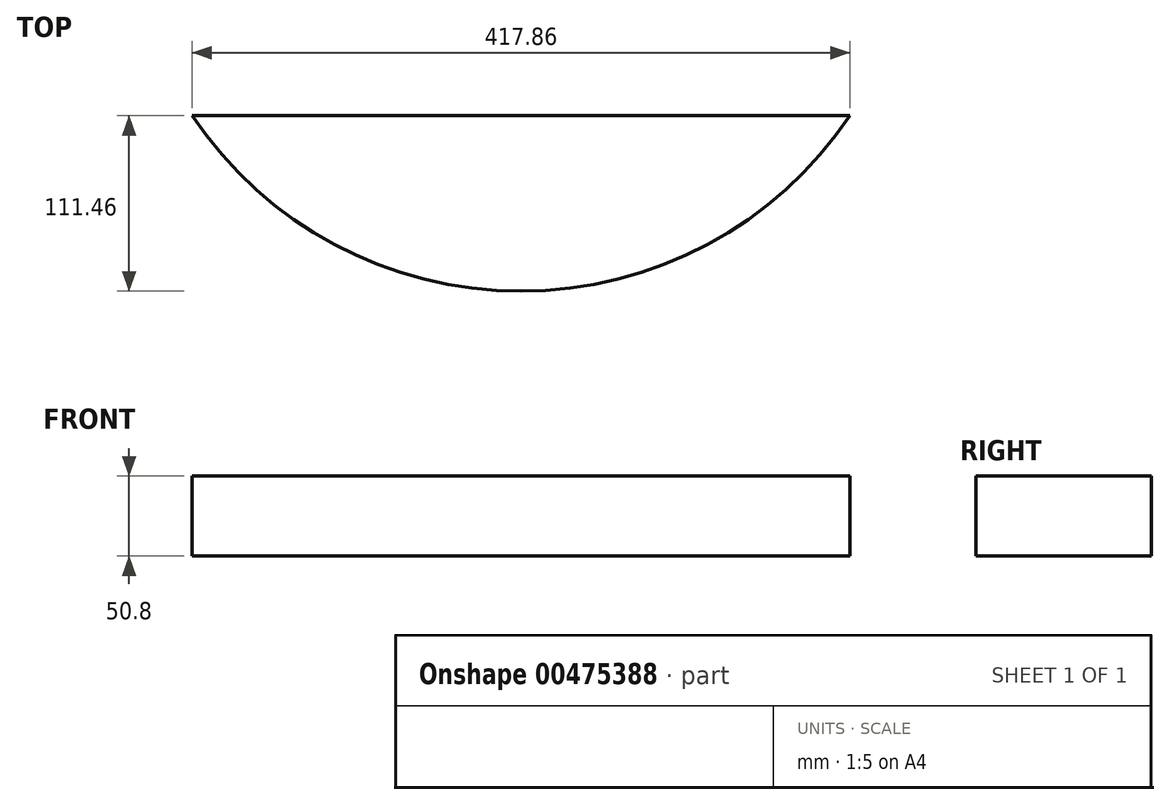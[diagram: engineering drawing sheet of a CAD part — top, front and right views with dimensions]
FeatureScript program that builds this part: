
annotation { "Feature Type Name" : "Feature", "Feature Type Description" : "" }
export const myFeature = defineFeature(function(context is Context, id is Id, definition is map)
    precondition{}
    {
        {
            var Q0;
            Q0=qCreatedBy(makeId("Top.planeOp"),FACE);
            var sketch = newSketch(context, id + "F0", { "sketchPlane" : qUnion([Q0])});
            skLineSegment(sketch, "E0.bottom", {"start": v(-194.6, -307.75) * mm, "end": v(216.92, -307.75) * mm});
            skLineSegment(sketch, "E0.top", {"start": v(-200.94, -104.18) * mm, "end": v(216.92, -104.18) * mm});
            skLineSegment(sketch, "E0.left", {"start": v(-200.94, -301.4) * mm, "end": v(-200.94, -104.18) * mm});
            skLineSegment(sketch, "E0.right", {"start": v(216.92, -307.75) * mm, "end": v(216.92, -104.18) * mm});
            skArc(sketch, "E1", {"start": v(-200.94, -104.18) * mm, "mid": v(7.99, -215.64) * mm, "end": v(216.92, -104.18) * mm});
            skPoint(sketch, "E2.visualSharp", {"position": v(-200.94, -307.75) * mm});
            skArc(sketch, "E2.filletArc", {"start": v(-200.94, -301.4) * mm, "mid": v(-199.08, -305.9) * mm, "end": v(-194.6, -307.75) * mm});
            skSolve(sketch);
        }
        {
            var Q0;
            Q0=makeQuery(id+"F0.imprint","IMPRINT",FACE,{"disambiguationData":[TD([[makeQuery(id+"F0.imprint","IMPRINT",EDGE,{"derivedFrom":sQuery(id+"F0.wireOp",EDGE,"E0.top")}),-1.0]])]});
            extrude(context, id + "F1", {"entities" : qUnion([Q0]), "depth" : 50.8 * mm});
        }
    });
